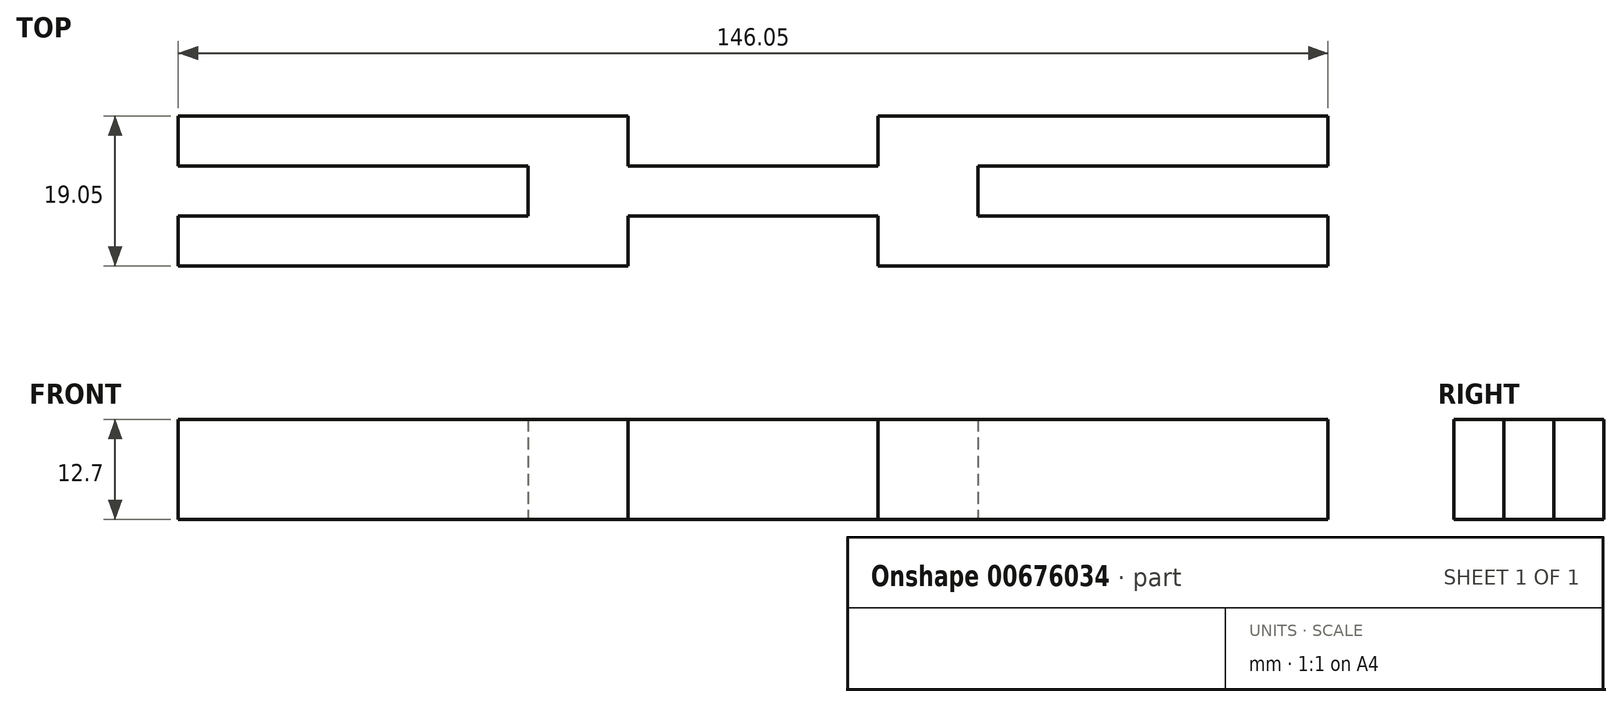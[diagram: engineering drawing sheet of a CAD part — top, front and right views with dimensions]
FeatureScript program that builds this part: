
annotation { "Feature Type Name" : "Feature", "Feature Type Description" : "" }
export const myFeature = defineFeature(function(context is Context, id is Id, definition is map)
    precondition{}
    {
        {
            var Q0;
            Q0=qCreatedBy(makeId("Top.planeOp"),FACE);
            var sketch = newSketch(context, id + "F0", { "sketchPlane" : qUnion([Q0])});
            skLineSegment(sketch, "E0.bottom", {"start": v(-77.54, 42.41) * mm, "end": v(-20.39, 42.41) * mm});
            skLineSegment(sketch, "E0.top", {"start": v(-77.54, 36.06) * mm, "end": v(-20.39, 36.06) * mm});
            skLineSegment(sketch, "E0.left", {"start": v(-77.54, 42.41) * mm, "end": v(-77.54, 36.06) * mm});
            skLineSegment(sketch, "E0.right", {"start": v(-20.39, 42.41) * mm, "end": v(-20.39, 36.06) * mm});
            skLineSegment(sketch, "E1.bottom", {"start": v(11.36, 42.41) * mm, "end": v(68.51, 42.41) * mm});
            skLineSegment(sketch, "E1.top", {"start": v(11.36, 36.06) * mm, "end": v(68.51, 36.06) * mm});
            skLineSegment(sketch, "E1.left", {"start": v(11.36, 42.41) * mm, "end": v(11.36, 36.06) * mm});
            skLineSegment(sketch, "E1.right", {"start": v(68.51, 42.41) * mm, "end": v(68.51, 36.06) * mm});
            skLineSegment(sketch, "E2.bottom", {"start": v(-33.09, 36.06) * mm, "end": v(24.06, 36.06) * mm});
            skLineSegment(sketch, "E2.top", {"start": v(-33.09, 29.71) * mm, "end": v(24.06, 29.71) * mm});
            skLineSegment(sketch, "E2.left", {"start": v(-33.09, 36.06) * mm, "end": v(-33.09, 29.71) * mm});
            skLineSegment(sketch, "E2.right", {"start": v(24.06, 36.06) * mm, "end": v(24.06, 29.71) * mm});
            skLineSegment(sketch, "E3.bottom", {"start": v(-20.39, 29.71) * mm, "end": v(-77.54, 29.71) * mm});
            skLineSegment(sketch, "E3.top", {"start": v(-20.39, 23.36) * mm, "end": v(-77.54, 23.36) * mm});
            skLineSegment(sketch, "E3.left", {"start": v(-20.39, 29.71) * mm, "end": v(-20.39, 23.36) * mm});
            skLineSegment(sketch, "E3.right", {"start": v(-77.54, 29.71) * mm, "end": v(-77.54, 23.36) * mm});
            skLineSegment(sketch, "E4.bottom", {"start": v(11.36, 29.71) * mm, "end": v(68.51, 29.71) * mm});
            skLineSegment(sketch, "E4.top", {"start": v(11.36, 23.36) * mm, "end": v(68.51, 23.36) * mm});
            skLineSegment(sketch, "E4.left", {"start": v(11.36, 29.71) * mm, "end": v(11.36, 23.36) * mm});
            skLineSegment(sketch, "E4.right", {"start": v(68.51, 29.71) * mm, "end": v(68.51, 23.36) * mm});
            skSolve(sketch);
        }
        {
            var Q0;
            Q0 = qSketchRegion(id + "F0", true);
            extrude(context, id + "F1", {"entities" : qUnion([Q0]), "depth" : 12.7 * mm, "offsetDistance" : 25.4 * mm});
        }
    });
